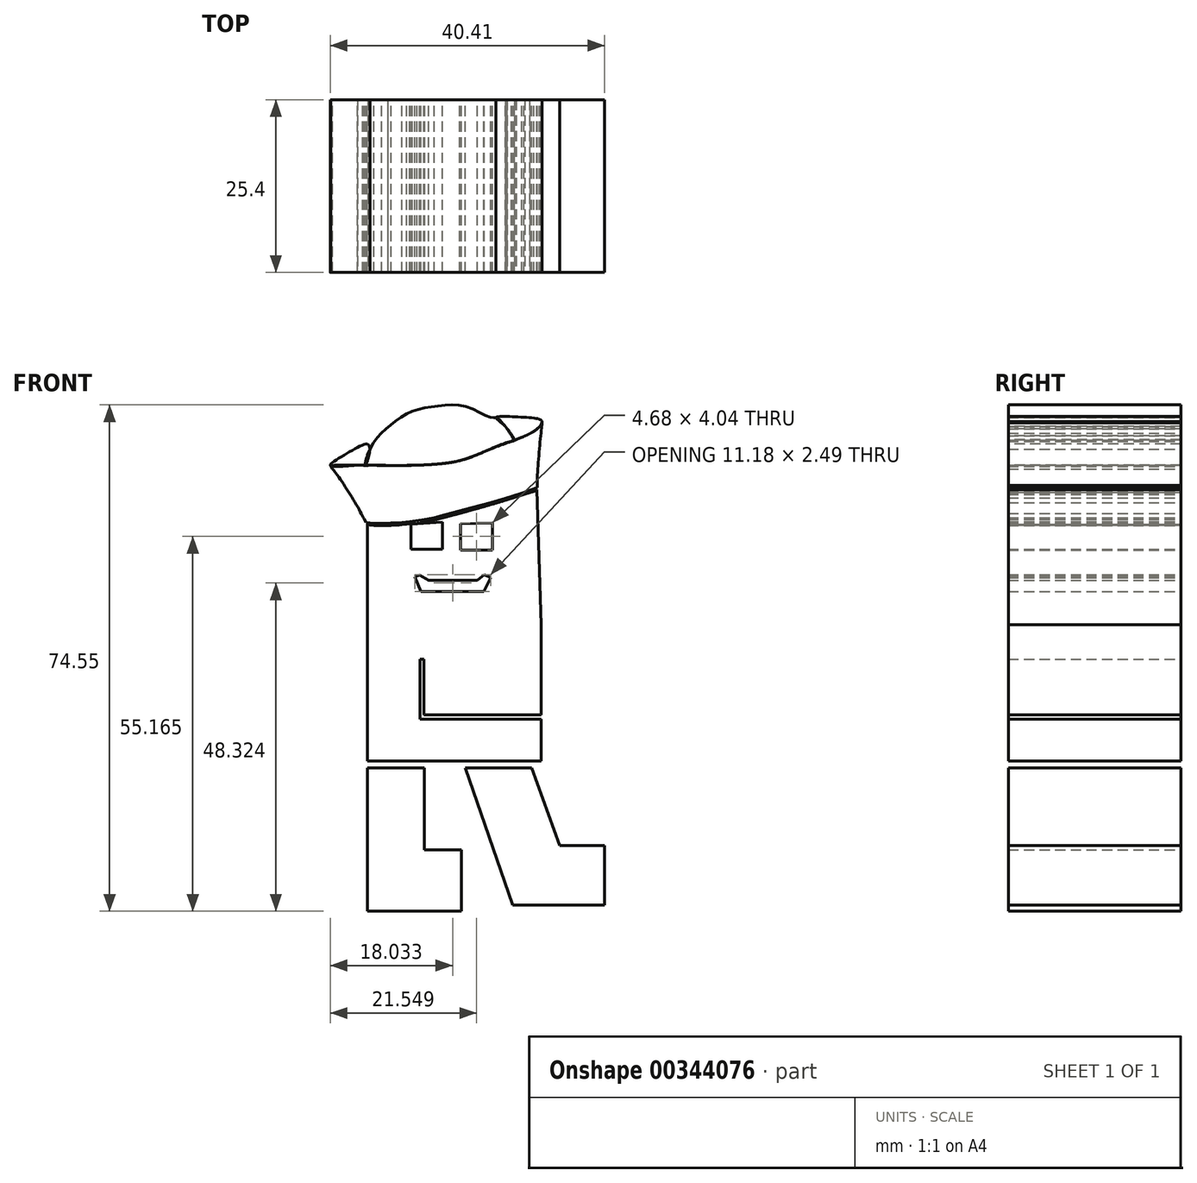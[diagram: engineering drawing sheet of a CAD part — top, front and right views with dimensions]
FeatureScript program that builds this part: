
annotation { "Feature Type Name" : "Feature", "Feature Type Description" : "" }
export const myFeature = defineFeature(function(context is Context, id is Id, definition is map)
    precondition{}
    {
        {
            var Q0;
            Q0=qCreatedBy(makeId("Front.planeOp"),FACE);
            var sketch = newSketch(context, id + "F0", { "sketchPlane" : qUnion([Q0])});
            skLineSegment(sketch, "E0", {"start": v(-88.68, 24.26) * mm, "end": v(-88.68, 9.5) * mm});
            skLineSegment(sketch, "E1", {"start": v(-88.68, -11) * mm, "end": v(-88.68, -32.7) * mm});
            skLineSegment(sketch, "E2", {"start": v(-88.68, -32.7) * mm, "end": v(-74.81, -32.7) * mm});
            skLineSegment(sketch, "E3", {"start": v(-74.81, -32.7) * mm, "end": v(-74.81, -23.66) * mm});
            skLineSegment(sketch, "E4", {"start": v(-74.81, -23.66) * mm, "end": v(-80.24, -23.66) * mm});
            skLineSegment(sketch, "E5", {"start": v(-80.24, -23.66) * mm, "end": v(-80.24, -11.6) * mm});
            skLineSegment(sketch, "E6", {"start": v(-80.24, -11.6) * mm, "end": v(-63.06, -11.6) * mm});
            skLineSegment(sketch, "E7", {"start": v(-63.06, -11.6) * mm, "end": v(-63.06, 9.5) * mm});
            skLineSegment(sketch, "E8", {"start": v(-63.06, 9.5) * mm, "end": v(-88.68, 9.5) * mm});
            skLineSegment(sketch, "E9", {"start": v(-88.68, 0) * mm, "end": v(-88.68, -11) * mm});
            skLineSegment(sketch, "E10", {"start": v(-88.68, 9.5) * mm, "end": v(-88.68, 0) * mm});
            skLineSegment(sketch, "E11", {"start": v(-63.66, 29.38) * mm, "end": v(-63.06, 9.5) * mm});
            skLineSegment(sketch, "E12", {"start": v(-67.28, -31.8) * mm, "end": v(-53.72, -31.8) * mm});
            skLineSegment(sketch, "E13", {"start": v(-53.72, -31.8) * mm, "end": v(-53.72, -23.05) * mm});
            skLineSegment(sketch, "E14", {"start": v(-53.72, -23.05) * mm, "end": v(-60.35, -23.05) * mm});
            skLineSegment(sketch, "E15", {"start": v(-60.35, -23.05) * mm, "end": v(-64.48, -11.6) * mm});
            skLineSegment(sketch, "E16", {"start": v(-64.48, -11.6) * mm, "end": v(-71.65, -11.6) * mm});
            skLineSegment(sketch, "E17", {"start": v(-80.88, 4.41) * mm, "end": v(-80.88, -4.44) * mm});
            skLineSegment(sketch, "E18", {"start": v(-80.88, -4.44) * mm, "end": v(-63.06, -4.44) * mm});
            skLineSegment(sketch, "E19", {"start": v(-63.06, -4.44) * mm, "end": v(-80.88, -4.44) * mm});
            skLineSegment(sketch, "E20", {"start": v(-82.23, 24.26) * mm, "end": v(-82.23, 20.6) * mm});
            skLineSegment(sketch, "E21", {"start": v(-82.23, 20.6) * mm, "end": v(-77.62, 20.6) * mm});
            skLineSegment(sketch, "E22", {"start": v(-77.62, 20.6) * mm, "end": v(-77.62, 24.6) * mm});
            skLineSegment(sketch, "E23", {"start": v(-77.62, 24.6) * mm, "end": v(-82.23, 24.26) * mm});
            skLineSegment(sketch, "E24", {"start": v(-74.92, 24.36) * mm, "end": v(-74.92, 20.44) * mm});
            skLineSegment(sketch, "E25", {"start": v(-74.92, 20.44) * mm, "end": v(-70.24, 20.45) * mm});
            skLineSegment(sketch, "E26", {"start": v(-70.24, 20.45) * mm, "end": v(-70.24, 24.49) * mm});
            skLineSegment(sketch, "E27", {"start": v(-70.24, 24.49) * mm, "end": v(-74.92, 24.36) * mm});
            skLineSegment(sketch, "E28", {"start": v(-81.69, 16.53) * mm, "end": v(-80.8, 14.38) * mm});
            skLineSegment(sketch, "E29", {"start": v(-80.8, 14.38) * mm, "end": v(-71.52, 14.38) * mm});
            skLineSegment(sketch, "E30", {"start": v(-71.52, 14.38) * mm, "end": v(-70.5, 16.41) * mm});
            skLineSegment(sketch, "E31", {"start": v(-70.5, 16.41) * mm, "end": v(-71.42, 16.87) * mm});
            skLineSegment(sketch, "E32", {"start": v(-71.42, 16.87) * mm, "end": v(-72.48, 16) * mm});
            skLineSegment(sketch, "E33", {"start": v(-72.48, 16) * mm, "end": v(-79.65, 16) * mm});
            skLineSegment(sketch, "E34", {"start": v(-79.65, 16) * mm, "end": v(-80.97, 16.77) * mm});
            skLineSegment(sketch, "E35", {"start": v(-80.97, 16.77) * mm, "end": v(-81.69, 16.53) * mm});
            skLineSegment(sketch, "E36", {"start": v(-62.91, 39.4) * mm, "end": v(-63.66, 29.38) * mm});
            skLineSegment(sketch, "E37", {"start": v(-94.06, 32.86) * mm, "end": v(-88.68, 24.26) * mm});
            skPoint(sketch, "E38.6.internal.snap0", {"position": v(-63.29, 34.39) * mm});
            skFitSpline(sketch, "E38", {"points": [v(-88.68, 24.26) * mm, v(-82.83, 24.26) * mm, v(-75.78, 25.68) * mm, v(-63.66, 29.38) * mm, v(-63.62, 29.96) * mm, v(-62.91, 39.4) * mm, v(-63.29, 38.66) * mm, v(-70.15, 35.5) * mm, v(-77.62, 33.2) * mm, v(-94.06, 32.86) * mm, v(-93.78, 32.4) * mm, v(-89.18, 25.06) * mm, v(-88.68, 24.26) * mm]});
            skFitSpline(sketch, "E39", {"points": [v(-94.06, 32.86) * mm, v(-91.65, 34.7) * mm, v(-88.37, 35.84) * mm, v(-88.94, 32.95) * mm, v(-89.32, 32.95) * mm, v(-94.06, 32.86) * mm]});
            skFitSpline(sketch, "E40", {"points": [v(-69.7, 39.96) * mm, v(-66.1, 40.04) * mm, v(-62.91, 39.4) * mm, v(-64.66, 37.64) * mm, v(-66.76, 36.73) * mm, v(-67, 36.64) * mm, v(-68.34, 38.66) * mm, v(-69.7, 39.96) * mm]});
            skFitSpline(sketch, "E41", {"points": [v(-88.94, 32.95) * mm, v(-87.97, 35.93) * mm, v(-85.54, 38.6) * mm, v(-82.35, 40.76) * mm, v(-78.48, 41.64) * mm, v(-74, 41.56) * mm, v(-70.41, 39.96) * mm, v(-69.7, 39.96) * mm, v(-68.34, 38.66) * mm, v(-67, 36.64) * mm, v(-67.47, 36.47) * mm, v(-71.33, 35) * mm, v(-75.64, 33.5) * mm, v(-80.95, 32.98) * mm, v(-85.62, 32.92) * mm, v(-88.45, 32.94) * mm, v(-88.94, 32.95) * mm]});
            skLineSegment(sketch, "E42", {"start": v(-74.25, -11.6) * mm, "end": v(-67.28, -31.8) * mm});
            skLineSegment(sketch, "E43", {"start": v(-80.24, -11.6) * mm, "end": v(-88.68, -11.6) * mm});
            skLineSegment(sketch, "E44", {"start": v(-80.88, 4.41) * mm, "end": v(-80.3, 4.41) * mm});
            skLineSegment(sketch, "E45", {"start": v(-80.3, 4.41) * mm, "end": v(-80.3, -3.8) * mm});
            skLineSegment(sketch, "E46", {"start": v(-80.3, -3.8) * mm, "end": v(-63.06, -3.8) * mm});
            skLineSegment(sketch, "E47", {"start": v(-63.06, -3.8) * mm, "end": v(-63.06, -4.44) * mm});
            skLineSegment(sketch, "E48", {"start": v(-63.06, -10.58) * mm, "end": v(-88.68, -10.58) * mm});
            skLineSegment(sketch, "E49", {"start": v(-88.68, 10.11) * mm, "end": v(-63.08, 10.11) * mm});
            skLineSegment(sketch, "E50", {"start": v(-88.68, 10.11) * mm, "end": v(-88.68, 9.5) * mm});
            skLineSegment(sketch, "E51", {"start": v(-63.08, 10.11) * mm, "end": v(-63.06, 9.5) * mm});
            skLineSegment(sketch, "E52", {"start": v(-88.86, 24.55) * mm, "end": v(-87.68, 24.41) * mm});
            skLineSegment(sketch, "E53", {"start": v(-87.68, 24.41) * mm, "end": v(-86.54, 24.42) * mm});
            skLineSegment(sketch, "E54", {"start": v(-86.54, 24.42) * mm, "end": v(-85.24, 24.47) * mm});
            skLineSegment(sketch, "E55", {"start": v(-85.24, 24.47) * mm, "end": v(-83.56, 24.53) * mm});
            skLineSegment(sketch, "E56", {"start": v(-83.56, 24.53) * mm, "end": v(-82.4, 24.62) * mm});
            skLineSegment(sketch, "E57", {"start": v(-82.4, 24.62) * mm, "end": v(-81.11, 24.83) * mm});
            skLineSegment(sketch, "E58", {"start": v(-81.11, 24.83) * mm, "end": v(-80.18, 24.98) * mm});
            skLineSegment(sketch, "E59", {"start": v(-80.18, 24.98) * mm, "end": v(-78.82, 25.25) * mm});
            skLineSegment(sketch, "E60", {"start": v(-78.82, 25.25) * mm, "end": v(-77.24, 25.65) * mm});
            skLineSegment(sketch, "E61", {"start": v(-77.24, 25.65) * mm, "end": v(-75.2, 26.19) * mm});
            skLineSegment(sketch, "E62", {"start": v(-75.2, 26.19) * mm, "end": v(-73.38, 26.67) * mm});
            skLineSegment(sketch, "E63", {"start": v(-73.38, 26.67) * mm, "end": v(-70.5, 27.43) * mm});
            skLineSegment(sketch, "E64", {"start": v(-70.5, 27.43) * mm, "end": v(-68.35, 28.1) * mm});
            skLineSegment(sketch, "E65", {"start": v(-68.35, 28.1) * mm, "end": v(-65.9, 28.87) * mm});
            skLineSegment(sketch, "E66", {"start": v(-65.9, 28.87) * mm, "end": v(-63.58, 29.7) * mm});
            skLineSegment(sketch, "E67", {"start": v(-63.58, 29.7) * mm, "end": v(-63.56, 29.51) * mm});
            skLineSegment(sketch, "E68", {"start": v(-63.56, 29.51) * mm, "end": v(-63.58, 29.46) * mm});
            skLineSegment(sketch, "E69", {"start": v(-63.58, 29.46) * mm, "end": v(-63.64, 29.38) * mm});
            skLineSegment(sketch, "E70", {"start": v(-63.64, 29.38) * mm, "end": v(-64.17, 29.1) * mm});
            skLineSegment(sketch, "E71", {"start": v(-64.17, 29.1) * mm, "end": v(-64.76, 28.92) * mm});
            skLineSegment(sketch, "E72", {"start": v(-64.76, 28.92) * mm, "end": v(-65.57, 28.63) * mm});
            skLineSegment(sketch, "E73", {"start": v(-65.57, 28.63) * mm, "end": v(-67.18, 28.12) * mm});
            skLineSegment(sketch, "E74", {"start": v(-67.18, 28.12) * mm, "end": v(-68.65, 27.7) * mm});
            skLineSegment(sketch, "E75", {"start": v(-68.65, 27.7) * mm, "end": v(-70.9, 27.04) * mm});
            skLineSegment(sketch, "E76", {"start": v(-70.9, 27.04) * mm, "end": v(-72.9, 26.47) * mm});
            skLineSegment(sketch, "E77", {"start": v(-72.9, 26.47) * mm, "end": v(-74.1, 26.14) * mm});
            skLineSegment(sketch, "E78", {"start": v(-74.1, 26.14) * mm, "end": v(-75.04, 25.88) * mm});
            skLineSegment(sketch, "E79", {"start": v(-75.04, 25.88) * mm, "end": v(-75.78, 25.68) * mm});
            skLineSegment(sketch, "E80", {"start": v(-75.78, 25.68) * mm, "end": v(-76.6, 25.46) * mm});
            skLineSegment(sketch, "E81", {"start": v(-76.6, 25.46) * mm, "end": v(-77.32, 25.27) * mm});
            skLineSegment(sketch, "E82", {"start": v(-77.32, 25.27) * mm, "end": v(-78.28, 25.03) * mm});
            skLineSegment(sketch, "E83", {"start": v(-78.28, 25.03) * mm, "end": v(-79.17, 24.83) * mm});
            skLineSegment(sketch, "E84", {"start": v(-79.17, 24.83) * mm, "end": v(-79.7, 24.7) * mm});
            skLineSegment(sketch, "E85", {"start": v(-79.7, 24.7) * mm, "end": v(-80.33, 24.6) * mm});
            skLineSegment(sketch, "E86", {"start": v(-80.33, 24.6) * mm, "end": v(-80.9, 24.5) * mm});
            skLineSegment(sketch, "E87", {"start": v(-80.9, 24.5) * mm, "end": v(-81.34, 24.42) * mm});
            skLineSegment(sketch, "E88", {"start": v(-81.34, 24.42) * mm, "end": v(-82.06, 24.33) * mm});
            skLineSegment(sketch, "E89", {"start": v(-82.06, 24.33) * mm, "end": v(-82.88, 24.25) * mm});
            skLineSegment(sketch, "E90", {"start": v(-82.88, 24.25) * mm, "end": v(-83.6, 24.2) * mm});
            skLineSegment(sketch, "E91", {"start": v(-83.6, 24.2) * mm, "end": v(-85.15, 24.1) * mm});
            skLineSegment(sketch, "E92", {"start": v(-85.15, 24.1) * mm, "end": v(-86.6, 24.08) * mm});
            skLineSegment(sketch, "E93", {"start": v(-86.6, 24.08) * mm, "end": v(-87.42, 24.1) * mm});
            skLineSegment(sketch, "E94", {"start": v(-87.42, 24.1) * mm, "end": v(-88.06, 24.14) * mm});
            skLineSegment(sketch, "E95", {"start": v(-88.06, 24.14) * mm, "end": v(-88.56, 24.22) * mm});
            skLineSegment(sketch, "E96", {"start": v(-88.56, 24.22) * mm, "end": v(-88.67, 24.26) * mm});
            skLineSegment(sketch, "E97", {"start": v(-88.67, 24.26) * mm, "end": v(-88.86, 24.55) * mm});
            skSolve(sketch);
        }
        {
            var Q0;
            {var subQ1=sQuery(id+"F0.wireOp",EDGE,"E0");Q0=makeQuery(id+"F0.imprint","IMPRINT",FACE,{"disambiguationData":[TD([[makeQuery(id+"F0.imprint","IMPRINT",EDGE,{"derivedFrom":subQ1}),1.0]])]});}
            var Q1;
            Q1=makeQuery(id+"F0.imprint","IMPRINT",FACE,{"disambiguationData":[TD([[makeQuery(id+"F0.imprint","IMPRINT",EDGE,{"derivedFrom":sQuery(id+"F0.wireOp",EDGE,"E1")}),1.0]])]});
            var Q2;
            Q2=makeQuery(id+"F0.imprint","IMPRINT",FACE,{"disambiguationData":[TD([[makeQuery(id+"F0.imprint","IMPRINT",EDGE,{"derivedFrom":sQuery(id+"F0.wireOp",EDGE,"89e0f370-7dde-42f9-8dba-64da66d548ce")}),1.0]])]});
            var Q3;
            {var subQ1=sQuery(id+"F0.wireOp",EDGE,"E38");var subQ12=sQuery(id+"F0.wireOp",EDGE,"E36");var subQ14=makeQuery(id+"F0.imprint","INTERSECT",VERTEX,{"derivedFrom":[subQ12,subQ1]});Q3=makeQuery(id+"F0.imprint","IMPRINT",FACE,{"disambiguationData":[TD([[makeQuery(id+"F0.imprint","IMPRINT",EDGE,{"disambiguationData":[TD([[subQ14,-1.0]])],"derivedFrom":subQ1}),1.0]])]});}
            var Q4;
            {var subQ0=sQuery(id+"F0.wireOp",EDGE,"E39");var subQ1=sQuery(id+"F0.wireOp",EDGE,"E38");var subQ6=makeQuery(id+"F0.imprint","INTERSECT",VERTEX,{"disambiguationData":[OD(0.0)],"derivedFrom":[subQ1,subQ0]});Q4=makeQuery(id+"F0.imprint","IMPRINT",FACE,{"disambiguationData":[TD([[makeQuery(id+"F0.imprint","IMPRINT",EDGE,{"disambiguationData":[TD([[subQ6,-1.0]])],"derivedFrom":subQ0}),-1.0]])]});}
            var Q5;
            {var subQ0=sQuery(id+"F0.wireOp",EDGE,"E41");var subQ6=sQuery(id+"F0.wireOp",EDGE,"E38");var subQ10=makeQuery(id+"F0.imprint","INTERSECT",VERTEX,{"disambiguationData":[OD(1.0)],"derivedFrom":[subQ6,subQ0]});Q5=makeQuery(id+"F0.imprint","IMPRINT",FACE,{"disambiguationData":[TD([[makeQuery(id+"F0.imprint","IMPRINT",EDGE,{"disambiguationData":[TD([[subQ10,-1.0]])],"derivedFrom":subQ6}),-1.0]])]});}
            var Q6;
            {var subQ0=sQuery(id+"F0.wireOp",EDGE,"E40");var subQ1=sQuery(id+"F0.wireOp",EDGE,"E38");var subQ2=makeQuery(id+"F0.imprint","INTERSECT",VERTEX,{"disambiguationData":[OD(0.0)],"derivedFrom":[subQ1,subQ0]});Q6=makeQuery(id+"F0.imprint","IMPRINT",FACE,{"disambiguationData":[TD([[makeQuery(id+"F0.imprint","IMPRINT",EDGE,{"disambiguationData":[TD([[subQ2,-1.0]])],"derivedFrom":subQ1}),-1.0]])]});}
            var Q7;
            Q7=makeQuery(id+"F0.imprint","IMPRINT",FACE,{"disambiguationData":[TD([[makeQuery(id+"F0.imprint","IMPRINT",EDGE,{"derivedFrom":sQuery(id+"F0.wireOp",EDGE,"61ecca4d-d67f-41e2-851f-e5ef2a28eb47")}),-1.0]])]});
            var Q8;
            Q8=makeQuery(id+"F0.imprint","IMPRINT",FACE,{"disambiguationData":[TD([[makeQuery(id+"F0.imprint","IMPRINT",EDGE,{"derivedFrom":sQuery(id+"F0.wireOp",EDGE,"c21fd5de-3064-40d1-b255-aa5974b88d94")}),1.0]])]});
            var Q9;
            Q9=makeQuery(id+"F0.imprint","IMPRINT",FACE,{"disambiguationData":[TD([[makeQuery(id+"F0.imprint","IMPRINT",EDGE,{"derivedFrom":sQuery(id+"F0.wireOp",EDGE,"6d0663a8-bb35-41d9-a97b-b67136c38158")}),-1.0]])]});
            var Q10;
            Q10=makeQuery(id+"F0.imprint","IMPRINT",FACE,{"disambiguationData":[TD([[makeQuery(id+"F0.imprint","IMPRINT",EDGE,{"derivedFrom":sQuery(id+"F0.wireOp",EDGE,"11c0735a-4b59-4939-8269-05a2cd191590")}),1.0]])]});
            var Q11;
            Q11=makeQuery(id+"F0.imprint","IMPRINT",FACE,{"disambiguationData":[TD([[makeQuery(id+"F0.imprint","IMPRINT",EDGE,{"derivedFrom":sQuery(id+"F0.wireOp",EDGE,"48bcd2fa-4d4f-436f-b074-460d14a134a7")}),1.0]])]});
            var Q12;
            Q12=makeQuery(id+"F0.imprint","IMPRINT",FACE,{"disambiguationData":[TD([[makeQuery(id+"F0.imprint","IMPRINT",EDGE,{"derivedFrom":sQuery(id+"F0.wireOp",EDGE,"1f9a4bdb-1be3-4fb7-b0d8-25e07f592b30")}),-1.0]])]});
            var Q13;
            Q13=makeQuery(id+"F0.imprint","IMPRINT",FACE,{"disambiguationData":[TD([[makeQuery(id+"F0.imprint","IMPRINT",EDGE,{"derivedFrom":sQuery(id+"F0.wireOp",EDGE,"562a7f39-ac6b-4889-b1fd-c4c05494213c")}),-1.0]])]});
            var Q14;
            Q14=makeQuery(id+"F0.imprint","IMPRINT",FACE,{"disambiguationData":[TD([[makeQuery(id+"F0.imprint","IMPRINT",EDGE,{"derivedFrom":sQuery(id+"F0.wireOp",EDGE,"f8f53ccf-7e53-465f-8331-383cac3894c2")}),-1.0]])]});
            var Q15;
            Q15=makeQuery(id+"F0.imprint","IMPRINT",FACE,{"disambiguationData":[TD([[makeQuery(id+"F0.imprint","IMPRINT",EDGE,{"derivedFrom":sQuery(id+"F0.wireOp",EDGE,"8291e4a1-eeb0-4b47-a153-f91d1c1eb4df")}),-1.0]])]});
            var Q16;
            {var subQ5=sQuery(id+"F0.wireOp",EDGE,"E8");Q16=makeQuery(id+"F0.imprint","IMPRINT",FACE,{"disambiguationData":[TD([[makeQuery(id+"F0.imprint","IMPRINT",EDGE,{"derivedFrom":subQ5}),1.0]])]});}
            var Q17;
            Q17=makeQuery(id+"F0.imprint","IMPRINT",FACE,{"disambiguationData":[TD([[makeQuery(id+"F0.imprint","IMPRINT",EDGE,{"derivedFrom":sQuery(id+"F0.wireOp",EDGE,"E12")}),1.0]])]});
            var Q18;
            Q18=makeQuery(id+"F0.imprint","IMPRINT",FACE,{"disambiguationData":[TD([[makeQuery(id+"F0.imprint","IMPRINT",EDGE,{"derivedFrom":sQuery(id+"F0.wireOp",EDGE,"E20")}),-1.0]])]});
            var Q19;
            Q19=makeQuery(id+"F0.imprint","IMPRINT",FACE,{"disambiguationData":[TD([[makeQuery(id+"F0.imprint","IMPRINT",EDGE,{"derivedFrom":sQuery(id+"F0.wireOp",EDGE,"b90e0925-664e-483f-852e-a9bf5860041c")}),1.0]])]});
            var Q20;
            Q20=makeQuery(id+"F0.imprint","IMPRINT",FACE,{"disambiguationData":[TD([[makeQuery(id+"F0.imprint","IMPRINT",EDGE,{"derivedFrom":sQuery(id+"F0.wireOp",EDGE,"14c8f392-fc46-426d-9ac4-9068f1b11302")}),1.0]])]});
            var Q21;
            Q21=makeQuery(id+"F0.imprint","IMPRINT",FACE,{"disambiguationData":[TD([[makeQuery(id+"F0.imprint","IMPRINT",EDGE,{"derivedFrom":sQuery(id+"F0.wireOp",EDGE,"6706f981-00ae-44ed-870c-2ce014d84a3d")}),1.0]])]});
            extrude(context, id + "F1", {"entities" : qUnion([Q0, Q1, Q2, Q3, Q4, Q5, Q6, Q7, Q8, Q9, Q10, Q11, Q12, Q13, Q14, Q15, Q16, Q17, Q18, Q19, Q20, Q21]), "depth" : 12.7 * mm, "hasSecondDirection" : true, "secondDirectionOppositeDirection" : true, "secondDirectionDepth" : 12.7 * mm});
        }
    });
